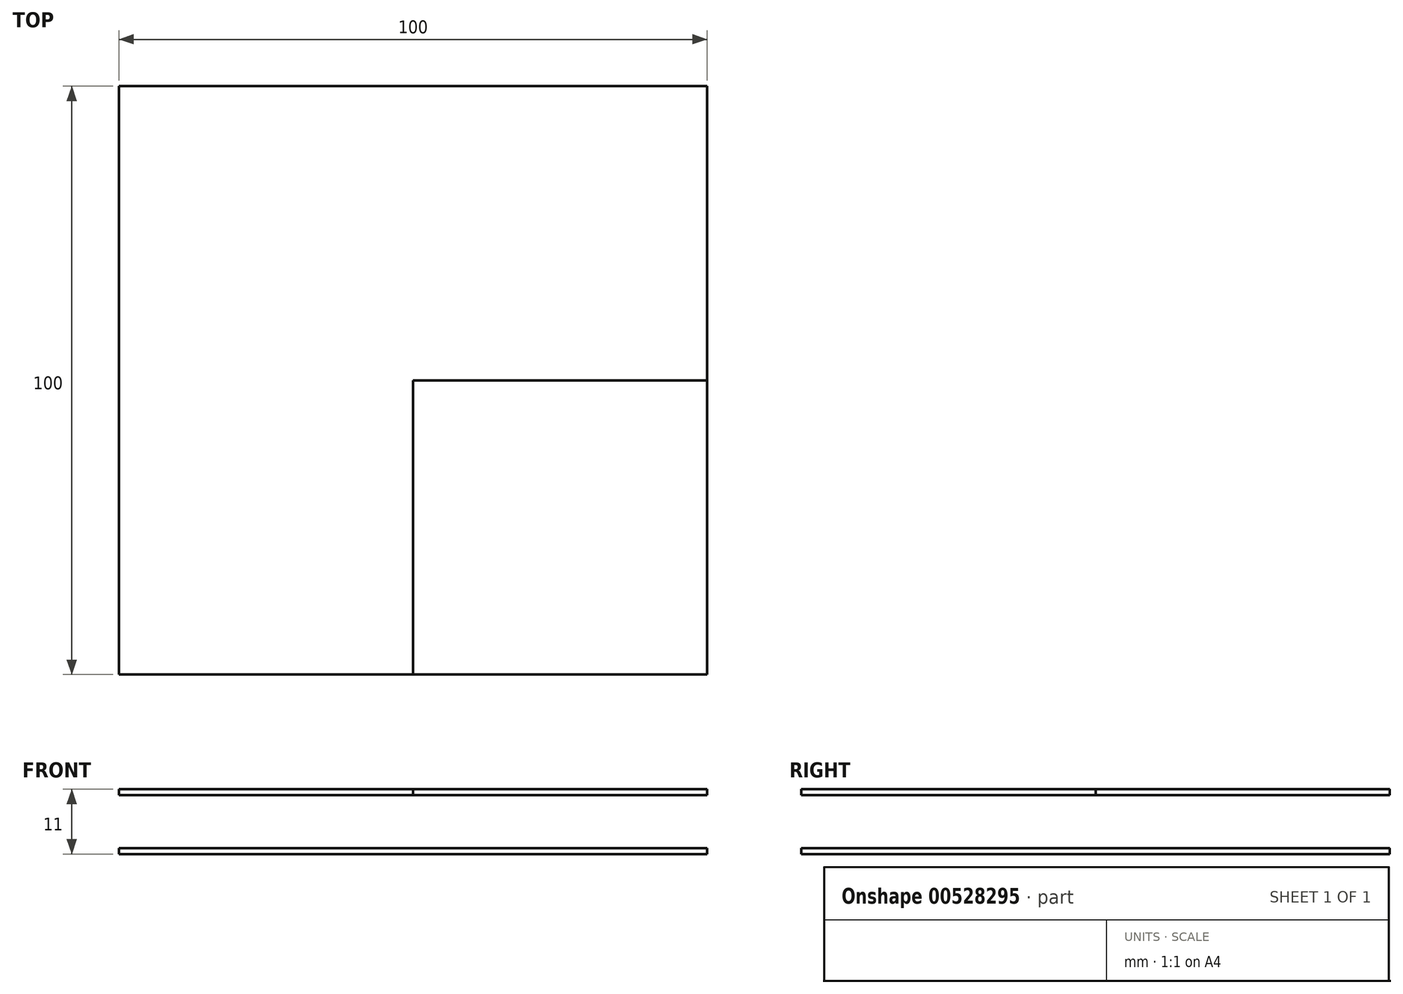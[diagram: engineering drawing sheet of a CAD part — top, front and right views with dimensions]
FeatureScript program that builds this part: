
annotation { "Feature Type Name" : "Feature", "Feature Type Description" : "" }
export const myFeature = defineFeature(function(context is Context, id is Id, definition is map)
    precondition{}
    {
        {
            var Q0;
            Q0=qCreatedBy(makeId("Top.planeOp"),FACE);
            var sketch = newSketch(context, id + "F0", { "sketchPlane" : qUnion([Q0])});
            skLineSegment(sketch, "E0.bottom", {"start": v(0, 0) * mm, "end": v(100, 0) * mm});
            skLineSegment(sketch, "E0.top", {"start": v(0, 100) * mm, "end": v(100, 100) * mm});
            skLineSegment(sketch, "E0.left", {"start": v(0, 0) * mm, "end": v(0, 100) * mm});
            skLineSegment(sketch, "E0.right", {"start": v(100, 0) * mm, "end": v(100, 100) * mm});
            skSolve(sketch);
        }
        {
            var Q0;
            Q0 = qSketchRegion(id + "F0", true);
            extrude(context, id + "F1", {"entities" : qUnion([Q0]), "depth" : 1 * mm, "offsetDistance" : 25 * mm});
        }
        {
            var Q0;
            Q0=qCreatedBy(makeId("Top.planeOp"),FACE);
            cPlane(context, id + "F2", {"entities" : qUnion([Q0]), "cplaneType" : CPlaneType.OFFSET, "offset" : 10 * mm, "width" : 150 * mm, "height" : 150 * mm});
        }
        {
            var Q0;
            Q0=qCreatedBy(id+"F2.planeOp",FACE);
            var sketch = newSketch(context, id + "F3", { "sketchPlane" : qUnion([Q0])});
            skLineSegment(sketch, "E1.bottom", {"start": v(0, 0) * mm, "end": v(100, 0) * mm});
            skLineSegment(sketch, "E1.top", {"start": v(0, 100) * mm, "end": v(100, 100) * mm});
            skLineSegment(sketch, "E1.left", {"start": v(0, 0) * mm, "end": v(0, 100) * mm});
            skLineSegment(sketch, "E1.right", {"start": v(100, 0) * mm, "end": v(100, 100) * mm});
            skLineSegment(sketch, "E2", {"start": v(50, 100) * mm, "end": v(50, 0) * mm});
            skLineSegment(sketch, "E3", {"start": v(0, 50) * mm, "end": v(100, 50) * mm});
            skSolve(sketch);
        }
        {
            var Q0;
            {var subQ0=sQuery(id+"F3.wireOp",EDGE,"E1.left");var subQ1=sQuery(id+"F3.wireOp",EDGE,"E1.bottom");var subQ2=makeQuery(id+"F3.imprint","INTERSECT",VERTEX,{"derivedFrom":[subQ1,subQ0]});Q0=makeQuery(id+"F3.imprint","IMPRINT",FACE,{"disambiguationData":[TD([[makeQuery(id+"F3.imprint","IMPRINT",EDGE,{"disambiguationData":[TD([[subQ2,-1.0]])],"derivedFrom":subQ1}),1.0]])]});}
            var Q1;
            {var subQ0=sQuery(id+"F3.wireOp",EDGE,"E1.left");var subQ1=sQuery(id+"F3.wireOp",EDGE,"E1.top");var subQ2=makeQuery(id+"F3.imprint","INTERSECT",VERTEX,{"derivedFrom":[subQ1,subQ0]});Q1=makeQuery(id+"F3.imprint","IMPRINT",FACE,{"disambiguationData":[TD([[makeQuery(id+"F3.imprint","IMPRINT",EDGE,{"disambiguationData":[TD([[subQ2,-1.0]])],"derivedFrom":subQ1}),-1.0]])]});}
            var Q2;
            {var subQ0=sQuery(id+"F3.wireOp",EDGE,"E1.right");var subQ1=sQuery(id+"F3.wireOp",EDGE,"E1.top");var subQ2=makeQuery(id+"F3.imprint","INTERSECT",VERTEX,{"derivedFrom":[subQ1,subQ0]});Q2=makeQuery(id+"F3.imprint","IMPRINT",FACE,{"disambiguationData":[TD([[makeQuery(id+"F3.imprint","IMPRINT",EDGE,{"disambiguationData":[TD([[subQ2,1.0]])],"derivedFrom":subQ1}),-1.0]])]});}
            extrude(context, id + "F4", {"entities" : qUnion([Q0, Q1, Q2]), "depth" : 1 * mm, "offsetDistance" : 25 * mm});
        }
        {
            var Q0;
            Q0=makeQuery(id+"F1.opExtrude","CAP_FACE",FACE,{"disambiguationData":[OSD([sQuery(id+"F0.wireOp",EDGE,"E0.bottom"),sQuery(id+"F0.wireOp",EDGE,"E0.top"),sQuery(id+"F0.wireOp",EDGE,"E0.left"),sQuery(id+"F0.wireOp",EDGE,"E0.right")])],"isStart":false});
            var sketch = newSketch(context, id + "F5", { "sketchPlane" : qUnion([Q0])});
            skLineSegment(sketch, "E4.bottom", {"start": v(96.5, 6.5) * mm, "end": v(93.5, 6.5) * mm});
            skLineSegment(sketch, "E4.top", {"start": v(96.5, 3.5) * mm, "end": v(93.5, 3.5) * mm});
            skLineSegment(sketch, "E4.left", {"start": v(96.5, 6.5) * mm, "end": v(96.5, 3.5) * mm});
            skLineSegment(sketch, "E4.right", {"start": v(93.5, 6.5) * mm, "end": v(93.5, 3.5) * mm});
            skPoint(sketch, "E4.middle", {"position": v(95, 5) * mm});
            skPoint(sketch, "E5.0.1.0", {"position": v(95, 15) * mm});
            skLineSegment(sketch, "E5.0.1.1", {"start": v(96.5, 16.5) * mm, "end": v(96.5, 13.5) * mm});
            skLineSegment(sketch, "E5.0.1.2", {"start": v(96.5, 16.5) * mm, "end": v(93.5, 16.5) * mm});
            skLineSegment(sketch, "E5.0.1.3", {"start": v(93.5, 16.5) * mm, "end": v(93.5, 13.5) * mm});
            skLineSegment(sketch, "E5.0.1.4", {"start": v(96.5, 13.5) * mm, "end": v(93.5, 13.5) * mm});
            skPoint(sketch, "E5.0.2.0", {"position": v(95, 25) * mm});
            skLineSegment(sketch, "E5.0.2.1", {"start": v(96.5, 26.5) * mm, "end": v(96.5, 23.5) * mm});
            skLineSegment(sketch, "E5.0.2.2", {"start": v(96.5, 26.5) * mm, "end": v(93.5, 26.5) * mm});
            skLineSegment(sketch, "E5.0.2.3", {"start": v(93.5, 26.5) * mm, "end": v(93.5, 23.5) * mm});
            skLineSegment(sketch, "E5.0.2.4", {"start": v(96.5, 23.5) * mm, "end": v(93.5, 23.5) * mm});
            skPoint(sketch, "E5.0.3.0", {"position": v(95, 35) * mm});
            skLineSegment(sketch, "E5.0.3.1", {"start": v(96.5, 36.5) * mm, "end": v(96.5, 33.5) * mm});
            skLineSegment(sketch, "E5.0.3.2", {"start": v(96.5, 36.5) * mm, "end": v(93.5, 36.5) * mm});
            skLineSegment(sketch, "E5.0.3.3", {"start": v(93.5, 36.5) * mm, "end": v(93.5, 33.5) * mm});
            skLineSegment(sketch, "E5.0.3.4", {"start": v(96.5, 33.5) * mm, "end": v(93.5, 33.5) * mm});
            skPoint(sketch, "E5.0.4.0", {"position": v(95, 45) * mm});
            skLineSegment(sketch, "E5.0.4.1", {"start": v(96.5, 46.5) * mm, "end": v(96.5, 43.5) * mm});
            skLineSegment(sketch, "E5.0.4.2", {"start": v(96.5, 46.5) * mm, "end": v(93.5, 46.5) * mm});
            skLineSegment(sketch, "E5.0.4.3", {"start": v(93.5, 46.5) * mm, "end": v(93.5, 43.5) * mm});
            skLineSegment(sketch, "E5.0.4.4", {"start": v(96.5, 43.5) * mm, "end": v(93.5, 43.5) * mm});
            skPoint(sketch, "E5.0.5.0", {"position": v(95, 55) * mm});
            skLineSegment(sketch, "E5.0.5.1", {"start": v(96.5, 56.5) * mm, "end": v(96.5, 53.5) * mm});
            skLineSegment(sketch, "E5.0.5.2", {"start": v(96.5, 56.5) * mm, "end": v(93.5, 56.5) * mm});
            skLineSegment(sketch, "E5.0.5.3", {"start": v(93.5, 56.5) * mm, "end": v(93.5, 53.5) * mm});
            skLineSegment(sketch, "E5.0.5.4", {"start": v(96.5, 53.5) * mm, "end": v(93.5, 53.5) * mm});
            skPoint(sketch, "E5.0.6.0", {"position": v(95, 65) * mm});
            skLineSegment(sketch, "E5.0.6.1", {"start": v(96.5, 66.5) * mm, "end": v(96.5, 63.5) * mm});
            skLineSegment(sketch, "E5.0.6.2", {"start": v(96.5, 66.5) * mm, "end": v(93.5, 66.5) * mm});
            skLineSegment(sketch, "E5.0.6.3", {"start": v(93.5, 66.5) * mm, "end": v(93.5, 63.5) * mm});
            skLineSegment(sketch, "E5.0.6.4", {"start": v(96.5, 63.5) * mm, "end": v(93.5, 63.5) * mm});
            skPoint(sketch, "E5.0.7.0", {"position": v(95, 75) * mm});
            skLineSegment(sketch, "E5.0.7.1", {"start": v(96.5, 76.5) * mm, "end": v(96.5, 73.5) * mm});
            skLineSegment(sketch, "E5.0.7.2", {"start": v(96.5, 76.5) * mm, "end": v(93.5, 76.5) * mm});
            skLineSegment(sketch, "E5.0.7.3", {"start": v(93.5, 76.5) * mm, "end": v(93.5, 73.5) * mm});
            skLineSegment(sketch, "E5.0.7.4", {"start": v(96.5, 73.5) * mm, "end": v(93.5, 73.5) * mm});
            skPoint(sketch, "E5.0.8.0", {"position": v(95, 85) * mm});
            skLineSegment(sketch, "E5.0.8.1", {"start": v(96.5, 86.5) * mm, "end": v(96.5, 83.5) * mm});
            skLineSegment(sketch, "E5.0.8.2", {"start": v(96.5, 86.5) * mm, "end": v(93.5, 86.5) * mm});
            skLineSegment(sketch, "E5.0.8.3", {"start": v(93.5, 86.5) * mm, "end": v(93.5, 83.5) * mm});
            skLineSegment(sketch, "E5.0.8.4", {"start": v(96.5, 83.5) * mm, "end": v(93.5, 83.5) * mm});
            skPoint(sketch, "E5.1.0.0", {"position": v(85, 5) * mm});
            skLineSegment(sketch, "E5.1.0.1", {"start": v(86.5, 6.5) * mm, "end": v(86.5, 3.5) * mm});
            skLineSegment(sketch, "E5.1.0.2", {"start": v(86.5, 6.5) * mm, "end": v(83.5, 6.5) * mm});
            skLineSegment(sketch, "E5.1.0.3", {"start": v(83.5, 6.5) * mm, "end": v(83.5, 3.5) * mm});
            skLineSegment(sketch, "E5.1.0.4", {"start": v(86.5, 3.5) * mm, "end": v(83.5, 3.5) * mm});
            skPoint(sketch, "E5.1.1.0", {"position": v(85, 15) * mm});
            skLineSegment(sketch, "E5.1.1.1", {"start": v(86.5, 16.5) * mm, "end": v(86.5, 13.5) * mm});
            skLineSegment(sketch, "E5.1.1.2", {"start": v(86.5, 16.5) * mm, "end": v(83.5, 16.5) * mm});
            skLineSegment(sketch, "E5.1.1.3", {"start": v(83.5, 16.5) * mm, "end": v(83.5, 13.5) * mm});
            skLineSegment(sketch, "E5.1.1.4", {"start": v(86.5, 13.5) * mm, "end": v(83.5, 13.5) * mm});
            skPoint(sketch, "E5.1.2.0", {"position": v(85, 25) * mm});
            skLineSegment(sketch, "E5.1.2.1", {"start": v(86.5, 26.5) * mm, "end": v(86.5, 23.5) * mm});
            skLineSegment(sketch, "E5.1.2.2", {"start": v(86.5, 26.5) * mm, "end": v(83.5, 26.5) * mm});
            skLineSegment(sketch, "E5.1.2.3", {"start": v(83.5, 26.5) * mm, "end": v(83.5, 23.5) * mm});
            skLineSegment(sketch, "E5.1.2.4", {"start": v(86.5, 23.5) * mm, "end": v(83.5, 23.5) * mm});
            skPoint(sketch, "E5.1.3.0", {"position": v(85, 35) * mm});
            skLineSegment(sketch, "E5.1.3.1", {"start": v(86.5, 36.5) * mm, "end": v(86.5, 33.5) * mm});
            skLineSegment(sketch, "E5.1.3.2", {"start": v(86.5, 36.5) * mm, "end": v(83.5, 36.5) * mm});
            skLineSegment(sketch, "E5.1.3.3", {"start": v(83.5, 36.5) * mm, "end": v(83.5, 33.5) * mm});
            skLineSegment(sketch, "E5.1.3.4", {"start": v(86.5, 33.5) * mm, "end": v(83.5, 33.5) * mm});
            skPoint(sketch, "E5.1.4.0", {"position": v(85, 45) * mm});
            skLineSegment(sketch, "E5.1.4.1", {"start": v(86.5, 46.5) * mm, "end": v(86.5, 43.5) * mm});
            skLineSegment(sketch, "E5.1.4.2", {"start": v(86.5, 46.5) * mm, "end": v(83.5, 46.5) * mm});
            skLineSegment(sketch, "E5.1.4.3", {"start": v(83.5, 46.5) * mm, "end": v(83.5, 43.5) * mm});
            skLineSegment(sketch, "E5.1.4.4", {"start": v(86.5, 43.5) * mm, "end": v(83.5, 43.5) * mm});
            skPoint(sketch, "E5.1.5.0", {"position": v(85, 55) * mm});
            skLineSegment(sketch, "E5.1.5.1", {"start": v(86.5, 56.5) * mm, "end": v(86.5, 53.5) * mm});
            skLineSegment(sketch, "E5.1.5.2", {"start": v(86.5, 56.5) * mm, "end": v(83.5, 56.5) * mm});
            skLineSegment(sketch, "E5.1.5.3", {"start": v(83.5, 56.5) * mm, "end": v(83.5, 53.5) * mm});
            skLineSegment(sketch, "E5.1.5.4", {"start": v(86.5, 53.5) * mm, "end": v(83.5, 53.5) * mm});
            skPoint(sketch, "E5.1.6.0", {"position": v(85, 65) * mm});
            skLineSegment(sketch, "E5.1.6.1", {"start": v(86.5, 66.5) * mm, "end": v(86.5, 63.5) * mm});
            skLineSegment(sketch, "E5.1.6.2", {"start": v(86.5, 66.5) * mm, "end": v(83.5, 66.5) * mm});
            skLineSegment(sketch, "E5.1.6.3", {"start": v(83.5, 66.5) * mm, "end": v(83.5, 63.5) * mm});
            skLineSegment(sketch, "E5.1.6.4", {"start": v(86.5, 63.5) * mm, "end": v(83.5, 63.5) * mm});
            skPoint(sketch, "E5.1.7.0", {"position": v(85, 75) * mm});
            skLineSegment(sketch, "E5.1.7.1", {"start": v(86.5, 76.5) * mm, "end": v(86.5, 73.5) * mm});
            skLineSegment(sketch, "E5.1.7.2", {"start": v(86.5, 76.5) * mm, "end": v(83.5, 76.5) * mm});
            skLineSegment(sketch, "E5.1.7.3", {"start": v(83.5, 76.5) * mm, "end": v(83.5, 73.5) * mm});
            skLineSegment(sketch, "E5.1.7.4", {"start": v(86.5, 73.5) * mm, "end": v(83.5, 73.5) * mm});
            skPoint(sketch, "E5.1.8.0", {"position": v(85, 85) * mm});
            skLineSegment(sketch, "E5.1.8.1", {"start": v(86.5, 86.5) * mm, "end": v(86.5, 83.5) * mm});
            skLineSegment(sketch, "E5.1.8.2", {"start": v(86.5, 86.5) * mm, "end": v(83.5, 86.5) * mm});
            skLineSegment(sketch, "E5.1.8.3", {"start": v(83.5, 86.5) * mm, "end": v(83.5, 83.5) * mm});
            skLineSegment(sketch, "E5.1.8.4", {"start": v(86.5, 83.5) * mm, "end": v(83.5, 83.5) * mm});
            skPoint(sketch, "E5.2.0.0", {"position": v(75, 5) * mm});
            skLineSegment(sketch, "E5.2.0.1", {"start": v(76.5, 6.5) * mm, "end": v(76.5, 3.5) * mm});
            skLineSegment(sketch, "E5.2.0.2", {"start": v(76.5, 6.5) * mm, "end": v(73.5, 6.5) * mm});
            skLineSegment(sketch, "E5.2.0.3", {"start": v(73.5, 6.5) * mm, "end": v(73.5, 3.5) * mm});
            skLineSegment(sketch, "E5.2.0.4", {"start": v(76.5, 3.5) * mm, "end": v(73.5, 3.5) * mm});
            skPoint(sketch, "E5.2.1.0", {"position": v(75, 15) * mm});
            skLineSegment(sketch, "E5.2.1.1", {"start": v(76.5, 16.5) * mm, "end": v(76.5, 13.5) * mm});
            skLineSegment(sketch, "E5.2.1.2", {"start": v(76.5, 16.5) * mm, "end": v(73.5, 16.5) * mm});
            skLineSegment(sketch, "E5.2.1.3", {"start": v(73.5, 16.5) * mm, "end": v(73.5, 13.5) * mm});
            skLineSegment(sketch, "E5.2.1.4", {"start": v(76.5, 13.5) * mm, "end": v(73.5, 13.5) * mm});
            skPoint(sketch, "E5.2.2.0", {"position": v(75, 25) * mm});
            skLineSegment(sketch, "E5.2.2.1", {"start": v(76.5, 26.5) * mm, "end": v(76.5, 23.5) * mm});
            skLineSegment(sketch, "E5.2.2.2", {"start": v(76.5, 26.5) * mm, "end": v(73.5, 26.5) * mm});
            skLineSegment(sketch, "E5.2.2.3", {"start": v(73.5, 26.5) * mm, "end": v(73.5, 23.5) * mm});
            skLineSegment(sketch, "E5.2.2.4", {"start": v(76.5, 23.5) * mm, "end": v(73.5, 23.5) * mm});
            skPoint(sketch, "E5.2.3.0", {"position": v(75, 35) * mm});
            skLineSegment(sketch, "E5.2.3.1", {"start": v(76.5, 36.5) * mm, "end": v(76.5, 33.5) * mm});
            skLineSegment(sketch, "E5.2.3.2", {"start": v(76.5, 36.5) * mm, "end": v(73.5, 36.5) * mm});
            skLineSegment(sketch, "E5.2.3.3", {"start": v(73.5, 36.5) * mm, "end": v(73.5, 33.5) * mm});
            skLineSegment(sketch, "E5.2.3.4", {"start": v(76.5, 33.5) * mm, "end": v(73.5, 33.5) * mm});
            skPoint(sketch, "E5.2.4.0", {"position": v(75, 45) * mm});
            skLineSegment(sketch, "E5.2.4.1", {"start": v(76.5, 46.5) * mm, "end": v(76.5, 43.5) * mm});
            skLineSegment(sketch, "E5.2.4.2", {"start": v(76.5, 46.5) * mm, "end": v(73.5, 46.5) * mm});
            skLineSegment(sketch, "E5.2.4.3", {"start": v(73.5, 46.5) * mm, "end": v(73.5, 43.5) * mm});
            skLineSegment(sketch, "E5.2.4.4", {"start": v(76.5, 43.5) * mm, "end": v(73.5, 43.5) * mm});
            skPoint(sketch, "E5.2.5.0", {"position": v(75, 55) * mm});
            skLineSegment(sketch, "E5.2.5.1", {"start": v(76.5, 56.5) * mm, "end": v(76.5, 53.5) * mm});
            skLineSegment(sketch, "E5.2.5.2", {"start": v(76.5, 56.5) * mm, "end": v(73.5, 56.5) * mm});
            skLineSegment(sketch, "E5.2.5.3", {"start": v(73.5, 56.5) * mm, "end": v(73.5, 53.5) * mm});
            skLineSegment(sketch, "E5.2.5.4", {"start": v(76.5, 53.5) * mm, "end": v(73.5, 53.5) * mm});
            skPoint(sketch, "E5.2.6.0", {"position": v(75, 65) * mm});
            skLineSegment(sketch, "E5.2.6.1", {"start": v(76.5, 66.5) * mm, "end": v(76.5, 63.5) * mm});
            skLineSegment(sketch, "E5.2.6.2", {"start": v(76.5, 66.5) * mm, "end": v(73.5, 66.5) * mm});
            skLineSegment(sketch, "E5.2.6.3", {"start": v(73.5, 66.5) * mm, "end": v(73.5, 63.5) * mm});
            skLineSegment(sketch, "E5.2.6.4", {"start": v(76.5, 63.5) * mm, "end": v(73.5, 63.5) * mm});
            skPoint(sketch, "E5.2.7.0", {"position": v(75, 75) * mm});
            skLineSegment(sketch, "E5.2.7.1", {"start": v(76.5, 76.5) * mm, "end": v(76.5, 73.5) * mm});
            skLineSegment(sketch, "E5.2.7.2", {"start": v(76.5, 76.5) * mm, "end": v(73.5, 76.5) * mm});
            skLineSegment(sketch, "E5.2.7.3", {"start": v(73.5, 76.5) * mm, "end": v(73.5, 73.5) * mm});
            skLineSegment(sketch, "E5.2.7.4", {"start": v(76.5, 73.5) * mm, "end": v(73.5, 73.5) * mm});
            skPoint(sketch, "E5.2.8.0", {"position": v(75, 85) * mm});
            skLineSegment(sketch, "E5.2.8.1", {"start": v(76.5, 86.5) * mm, "end": v(76.5, 83.5) * mm});
            skLineSegment(sketch, "E5.2.8.2", {"start": v(76.5, 86.5) * mm, "end": v(73.5, 86.5) * mm});
            skLineSegment(sketch, "E5.2.8.3", {"start": v(73.5, 86.5) * mm, "end": v(73.5, 83.5) * mm});
            skLineSegment(sketch, "E5.2.8.4", {"start": v(76.5, 83.5) * mm, "end": v(73.5, 83.5) * mm});
            skPoint(sketch, "E5.3.0.0", {"position": v(65, 5) * mm});
            skLineSegment(sketch, "E5.3.0.1", {"start": v(66.5, 6.5) * mm, "end": v(66.5, 3.5) * mm});
            skLineSegment(sketch, "E5.3.0.2", {"start": v(66.5, 6.5) * mm, "end": v(63.5, 6.5) * mm});
            skLineSegment(sketch, "E5.3.0.3", {"start": v(63.5, 6.5) * mm, "end": v(63.5, 3.5) * mm});
            skLineSegment(sketch, "E5.3.0.4", {"start": v(66.5, 3.5) * mm, "end": v(63.5, 3.5) * mm});
            skPoint(sketch, "E5.3.1.0", {"position": v(65, 15) * mm});
            skLineSegment(sketch, "E5.3.1.1", {"start": v(66.5, 16.5) * mm, "end": v(66.5, 13.5) * mm});
            skLineSegment(sketch, "E5.3.1.2", {"start": v(66.5, 16.5) * mm, "end": v(63.5, 16.5) * mm});
            skLineSegment(sketch, "E5.3.1.3", {"start": v(63.5, 16.5) * mm, "end": v(63.5, 13.5) * mm});
            skLineSegment(sketch, "E5.3.1.4", {"start": v(66.5, 13.5) * mm, "end": v(63.5, 13.5) * mm});
            skPoint(sketch, "E5.3.2.0", {"position": v(65, 25) * mm});
            skLineSegment(sketch, "E5.3.2.1", {"start": v(66.5, 26.5) * mm, "end": v(66.5, 23.5) * mm});
            skLineSegment(sketch, "E5.3.2.2", {"start": v(66.5, 26.5) * mm, "end": v(63.5, 26.5) * mm});
            skLineSegment(sketch, "E5.3.2.3", {"start": v(63.5, 26.5) * mm, "end": v(63.5, 23.5) * mm});
            skLineSegment(sketch, "E5.3.2.4", {"start": v(66.5, 23.5) * mm, "end": v(63.5, 23.5) * mm});
            skPoint(sketch, "E5.3.3.0", {"position": v(65, 35) * mm});
            skLineSegment(sketch, "E5.3.3.1", {"start": v(66.5, 36.5) * mm, "end": v(66.5, 33.5) * mm});
            skLineSegment(sketch, "E5.3.3.2", {"start": v(66.5, 36.5) * mm, "end": v(63.5, 36.5) * mm});
            skLineSegment(sketch, "E5.3.3.3", {"start": v(63.5, 36.5) * mm, "end": v(63.5, 33.5) * mm});
            skLineSegment(sketch, "E5.3.3.4", {"start": v(66.5, 33.5) * mm, "end": v(63.5, 33.5) * mm});
            skPoint(sketch, "E5.3.4.0", {"position": v(65, 45) * mm});
            skLineSegment(sketch, "E5.3.4.1", {"start": v(66.5, 46.5) * mm, "end": v(66.5, 43.5) * mm});
            skLineSegment(sketch, "E5.3.4.2", {"start": v(66.5, 46.5) * mm, "end": v(63.5, 46.5) * mm});
            skLineSegment(sketch, "E5.3.4.3", {"start": v(63.5, 46.5) * mm, "end": v(63.5, 43.5) * mm});
            skLineSegment(sketch, "E5.3.4.4", {"start": v(66.5, 43.5) * mm, "end": v(63.5, 43.5) * mm});
            skPoint(sketch, "E5.3.5.0", {"position": v(65, 55) * mm});
            skLineSegment(sketch, "E5.3.5.1", {"start": v(66.5, 56.5) * mm, "end": v(66.5, 53.5) * mm});
            skLineSegment(sketch, "E5.3.5.2", {"start": v(66.5, 56.5) * mm, "end": v(63.5, 56.5) * mm});
            skLineSegment(sketch, "E5.3.5.3", {"start": v(63.5, 56.5) * mm, "end": v(63.5, 53.5) * mm});
            skLineSegment(sketch, "E5.3.5.4", {"start": v(66.5, 53.5) * mm, "end": v(63.5, 53.5) * mm});
            skPoint(sketch, "E5.3.6.0", {"position": v(65, 65) * mm});
            skLineSegment(sketch, "E5.3.6.1", {"start": v(66.5, 66.5) * mm, "end": v(66.5, 63.5) * mm});
            skLineSegment(sketch, "E5.3.6.2", {"start": v(66.5, 66.5) * mm, "end": v(63.5, 66.5) * mm});
            skLineSegment(sketch, "E5.3.6.3", {"start": v(63.5, 66.5) * mm, "end": v(63.5, 63.5) * mm});
            skLineSegment(sketch, "E5.3.6.4", {"start": v(66.5, 63.5) * mm, "end": v(63.5, 63.5) * mm});
            skPoint(sketch, "E5.3.7.0", {"position": v(65, 75) * mm});
            skLineSegment(sketch, "E5.3.7.1", {"start": v(66.5, 76.5) * mm, "end": v(66.5, 73.5) * mm});
            skLineSegment(sketch, "E5.3.7.2", {"start": v(66.5, 76.5) * mm, "end": v(63.5, 76.5) * mm});
            skLineSegment(sketch, "E5.3.7.3", {"start": v(63.5, 76.5) * mm, "end": v(63.5, 73.5) * mm});
            skLineSegment(sketch, "E5.3.7.4", {"start": v(66.5, 73.5) * mm, "end": v(63.5, 73.5) * mm});
            skPoint(sketch, "E5.3.8.0", {"position": v(65, 85) * mm});
            skLineSegment(sketch, "E5.3.8.1", {"start": v(66.5, 86.5) * mm, "end": v(66.5, 83.5) * mm});
            skLineSegment(sketch, "E5.3.8.2", {"start": v(66.5, 86.5) * mm, "end": v(63.5, 86.5) * mm});
            skLineSegment(sketch, "E5.3.8.3", {"start": v(63.5, 86.5) * mm, "end": v(63.5, 83.5) * mm});
            skLineSegment(sketch, "E5.3.8.4", {"start": v(66.5, 83.5) * mm, "end": v(63.5, 83.5) * mm});
            skPoint(sketch, "E5.4.0.0", {"position": v(55, 5) * mm});
            skLineSegment(sketch, "E5.4.0.1", {"start": v(56.5, 6.5) * mm, "end": v(56.5, 3.5) * mm});
            skLineSegment(sketch, "E5.4.0.2", {"start": v(56.5, 6.5) * mm, "end": v(53.5, 6.5) * mm});
            skLineSegment(sketch, "E5.4.0.3", {"start": v(53.5, 6.5) * mm, "end": v(53.5, 3.5) * mm});
            skLineSegment(sketch, "E5.4.0.4", {"start": v(56.5, 3.5) * mm, "end": v(53.5, 3.5) * mm});
            skPoint(sketch, "E5.4.1.0", {"position": v(55, 15) * mm});
            skLineSegment(sketch, "E5.4.1.1", {"start": v(56.5, 16.5) * mm, "end": v(56.5, 13.5) * mm});
            skLineSegment(sketch, "E5.4.1.2", {"start": v(56.5, 16.5) * mm, "end": v(53.5, 16.5) * mm});
            skLineSegment(sketch, "E5.4.1.3", {"start": v(53.5, 16.5) * mm, "end": v(53.5, 13.5) * mm});
            skLineSegment(sketch, "E5.4.1.4", {"start": v(56.5, 13.5) * mm, "end": v(53.5, 13.5) * mm});
            skPoint(sketch, "E5.4.2.0", {"position": v(55, 25) * mm});
            skLineSegment(sketch, "E5.4.2.1", {"start": v(56.5, 26.5) * mm, "end": v(56.5, 23.5) * mm});
            skLineSegment(sketch, "E5.4.2.2", {"start": v(56.5, 26.5) * mm, "end": v(53.5, 26.5) * mm});
            skLineSegment(sketch, "E5.4.2.3", {"start": v(53.5, 26.5) * mm, "end": v(53.5, 23.5) * mm});
            skLineSegment(sketch, "E5.4.2.4", {"start": v(56.5, 23.5) * mm, "end": v(53.5, 23.5) * mm});
            skPoint(sketch, "E5.4.3.0", {"position": v(55, 35) * mm});
            skLineSegment(sketch, "E5.4.3.1", {"start": v(56.5, 36.5) * mm, "end": v(56.5, 33.5) * mm});
            skLineSegment(sketch, "E5.4.3.2", {"start": v(56.5, 36.5) * mm, "end": v(53.5, 36.5) * mm});
            skLineSegment(sketch, "E5.4.3.3", {"start": v(53.5, 36.5) * mm, "end": v(53.5, 33.5) * mm});
            skLineSegment(sketch, "E5.4.3.4", {"start": v(56.5, 33.5) * mm, "end": v(53.5, 33.5) * mm});
            skPoint(sketch, "E5.4.4.0", {"position": v(55, 45) * mm});
            skLineSegment(sketch, "E5.4.4.1", {"start": v(56.5, 46.5) * mm, "end": v(56.5, 43.5) * mm});
            skLineSegment(sketch, "E5.4.4.2", {"start": v(56.5, 46.5) * mm, "end": v(53.5, 46.5) * mm});
            skLineSegment(sketch, "E5.4.4.3", {"start": v(53.5, 46.5) * mm, "end": v(53.5, 43.5) * mm});
            skLineSegment(sketch, "E5.4.4.4", {"start": v(56.5, 43.5) * mm, "end": v(53.5, 43.5) * mm});
            skPoint(sketch, "E5.4.5.0", {"position": v(55, 55) * mm});
            skLineSegment(sketch, "E5.4.5.1", {"start": v(56.5, 56.5) * mm, "end": v(56.5, 53.5) * mm});
            skLineSegment(sketch, "E5.4.5.2", {"start": v(56.5, 56.5) * mm, "end": v(53.5, 56.5) * mm});
            skLineSegment(sketch, "E5.4.5.3", {"start": v(53.5, 56.5) * mm, "end": v(53.5, 53.5) * mm});
            skLineSegment(sketch, "E5.4.5.4", {"start": v(56.5, 53.5) * mm, "end": v(53.5, 53.5) * mm});
            skPoint(sketch, "E5.4.6.0", {"position": v(55, 65) * mm});
            skLineSegment(sketch, "E5.4.6.1", {"start": v(56.5, 66.5) * mm, "end": v(56.5, 63.5) * mm});
            skLineSegment(sketch, "E5.4.6.2", {"start": v(56.5, 66.5) * mm, "end": v(53.5, 66.5) * mm});
            skLineSegment(sketch, "E5.4.6.3", {"start": v(53.5, 66.5) * mm, "end": v(53.5, 63.5) * mm});
            skLineSegment(sketch, "E5.4.6.4", {"start": v(56.5, 63.5) * mm, "end": v(53.5, 63.5) * mm});
            skPoint(sketch, "E5.4.7.0", {"position": v(55, 75) * mm});
            skLineSegment(sketch, "E5.4.7.1", {"start": v(56.5, 76.5) * mm, "end": v(56.5, 73.5) * mm});
            skLineSegment(sketch, "E5.4.7.2", {"start": v(56.5, 76.5) * mm, "end": v(53.5, 76.5) * mm});
            skLineSegment(sketch, "E5.4.7.3", {"start": v(53.5, 76.5) * mm, "end": v(53.5, 73.5) * mm});
            skLineSegment(sketch, "E5.4.7.4", {"start": v(56.5, 73.5) * mm, "end": v(53.5, 73.5) * mm});
            skPoint(sketch, "E5.4.8.0", {"position": v(55, 85) * mm});
            skLineSegment(sketch, "E5.4.8.1", {"start": v(56.5, 86.5) * mm, "end": v(56.5, 83.5) * mm});
            skLineSegment(sketch, "E5.4.8.2", {"start": v(56.5, 86.5) * mm, "end": v(53.5, 86.5) * mm});
            skLineSegment(sketch, "E5.4.8.3", {"start": v(53.5, 86.5) * mm, "end": v(53.5, 83.5) * mm});
            skLineSegment(sketch, "E5.4.8.4", {"start": v(56.5, 83.5) * mm, "end": v(53.5, 83.5) * mm});
            skPoint(sketch, "E5.5.0.0", {"position": v(45, 5) * mm});
            skLineSegment(sketch, "E5.5.0.1", {"start": v(46.5, 6.5) * mm, "end": v(46.5, 3.5) * mm});
            skLineSegment(sketch, "E5.5.0.2", {"start": v(46.5, 6.5) * mm, "end": v(43.5, 6.5) * mm});
            skLineSegment(sketch, "E5.5.0.3", {"start": v(43.5, 6.5) * mm, "end": v(43.5, 3.5) * mm});
            skLineSegment(sketch, "E5.5.0.4", {"start": v(46.5, 3.5) * mm, "end": v(43.5, 3.5) * mm});
            skPoint(sketch, "E5.5.1.0", {"position": v(45, 15) * mm});
            skLineSegment(sketch, "E5.5.1.1", {"start": v(46.5, 16.5) * mm, "end": v(46.5, 13.5) * mm});
            skLineSegment(sketch, "E5.5.1.2", {"start": v(46.5, 16.5) * mm, "end": v(43.5, 16.5) * mm});
            skLineSegment(sketch, "E5.5.1.3", {"start": v(43.5, 16.5) * mm, "end": v(43.5, 13.5) * mm});
            skLineSegment(sketch, "E5.5.1.4", {"start": v(46.5, 13.5) * mm, "end": v(43.5, 13.5) * mm});
            skPoint(sketch, "E5.5.2.0", {"position": v(45, 25) * mm});
            skLineSegment(sketch, "E5.5.2.1", {"start": v(46.5, 26.5) * mm, "end": v(46.5, 23.5) * mm});
            skLineSegment(sketch, "E5.5.2.2", {"start": v(46.5, 26.5) * mm, "end": v(43.5, 26.5) * mm});
            skLineSegment(sketch, "E5.5.2.3", {"start": v(43.5, 26.5) * mm, "end": v(43.5, 23.5) * mm});
            skLineSegment(sketch, "E5.5.2.4", {"start": v(46.5, 23.5) * mm, "end": v(43.5, 23.5) * mm});
            skPoint(sketch, "E5.5.3.0", {"position": v(45, 35) * mm});
            skLineSegment(sketch, "E5.5.3.1", {"start": v(46.5, 36.5) * mm, "end": v(46.5, 33.5) * mm});
            skLineSegment(sketch, "E5.5.3.2", {"start": v(46.5, 36.5) * mm, "end": v(43.5, 36.5) * mm});
            skLineSegment(sketch, "E5.5.3.3", {"start": v(43.5, 36.5) * mm, "end": v(43.5, 33.5) * mm});
            skLineSegment(sketch, "E5.5.3.4", {"start": v(46.5, 33.5) * mm, "end": v(43.5, 33.5) * mm});
            skPoint(sketch, "E5.5.4.0", {"position": v(45, 45) * mm});
            skLineSegment(sketch, "E5.5.4.1", {"start": v(46.5, 46.5) * mm, "end": v(46.5, 43.5) * mm});
            skLineSegment(sketch, "E5.5.4.2", {"start": v(46.5, 46.5) * mm, "end": v(43.5, 46.5) * mm});
            skLineSegment(sketch, "E5.5.4.3", {"start": v(43.5, 46.5) * mm, "end": v(43.5, 43.5) * mm});
            skLineSegment(sketch, "E5.5.4.4", {"start": v(46.5, 43.5) * mm, "end": v(43.5, 43.5) * mm});
            skPoint(sketch, "E5.5.5.0", {"position": v(45, 55) * mm});
            skLineSegment(sketch, "E5.5.5.1", {"start": v(46.5, 56.5) * mm, "end": v(46.5, 53.5) * mm});
            skLineSegment(sketch, "E5.5.5.2", {"start": v(46.5, 56.5) * mm, "end": v(43.5, 56.5) * mm});
            skLineSegment(sketch, "E5.5.5.3", {"start": v(43.5, 56.5) * mm, "end": v(43.5, 53.5) * mm});
            skLineSegment(sketch, "E5.5.5.4", {"start": v(46.5, 53.5) * mm, "end": v(43.5, 53.5) * mm});
            skPoint(sketch, "E5.5.6.0", {"position": v(45, 65) * mm});
            skLineSegment(sketch, "E5.5.6.1", {"start": v(46.5, 66.5) * mm, "end": v(46.5, 63.5) * mm});
            skLineSegment(sketch, "E5.5.6.2", {"start": v(46.5, 66.5) * mm, "end": v(43.5, 66.5) * mm});
            skLineSegment(sketch, "E5.5.6.3", {"start": v(43.5, 66.5) * mm, "end": v(43.5, 63.5) * mm});
            skLineSegment(sketch, "E5.5.6.4", {"start": v(46.5, 63.5) * mm, "end": v(43.5, 63.5) * mm});
            skPoint(sketch, "E5.5.7.0", {"position": v(45, 75) * mm});
            skLineSegment(sketch, "E5.5.7.1", {"start": v(46.5, 76.5) * mm, "end": v(46.5, 73.5) * mm});
            skLineSegment(sketch, "E5.5.7.2", {"start": v(46.5, 76.5) * mm, "end": v(43.5, 76.5) * mm});
            skLineSegment(sketch, "E5.5.7.3", {"start": v(43.5, 76.5) * mm, "end": v(43.5, 73.5) * mm});
            skLineSegment(sketch, "E5.5.7.4", {"start": v(46.5, 73.5) * mm, "end": v(43.5, 73.5) * mm});
            skPoint(sketch, "E5.5.8.0", {"position": v(45, 85) * mm});
            skLineSegment(sketch, "E5.5.8.1", {"start": v(46.5, 86.5) * mm, "end": v(46.5, 83.5) * mm});
            skLineSegment(sketch, "E5.5.8.2", {"start": v(46.5, 86.5) * mm, "end": v(43.5, 86.5) * mm});
            skLineSegment(sketch, "E5.5.8.3", {"start": v(43.5, 86.5) * mm, "end": v(43.5, 83.5) * mm});
            skLineSegment(sketch, "E5.5.8.4", {"start": v(46.5, 83.5) * mm, "end": v(43.5, 83.5) * mm});
            skPoint(sketch, "E5.6.0.0", {"position": v(35, 5) * mm});
            skLineSegment(sketch, "E5.6.0.1", {"start": v(36.5, 6.5) * mm, "end": v(36.5, 3.5) * mm});
            skLineSegment(sketch, "E5.6.0.2", {"start": v(36.5, 6.5) * mm, "end": v(33.5, 6.5) * mm});
            skLineSegment(sketch, "E5.6.0.3", {"start": v(33.5, 6.5) * mm, "end": v(33.5, 3.5) * mm});
            skLineSegment(sketch, "E5.6.0.4", {"start": v(36.5, 3.5) * mm, "end": v(33.5, 3.5) * mm});
            skPoint(sketch, "E5.6.1.0", {"position": v(35, 15) * mm});
            skLineSegment(sketch, "E5.6.1.1", {"start": v(36.5, 16.5) * mm, "end": v(36.5, 13.5) * mm});
            skLineSegment(sketch, "E5.6.1.2", {"start": v(36.5, 16.5) * mm, "end": v(33.5, 16.5) * mm});
            skLineSegment(sketch, "E5.6.1.3", {"start": v(33.5, 16.5) * mm, "end": v(33.5, 13.5) * mm});
            skLineSegment(sketch, "E5.6.1.4", {"start": v(36.5, 13.5) * mm, "end": v(33.5, 13.5) * mm});
            skPoint(sketch, "E5.6.2.0", {"position": v(35, 25) * mm});
            skLineSegment(sketch, "E5.6.2.1", {"start": v(36.5, 26.5) * mm, "end": v(36.5, 23.5) * mm});
            skLineSegment(sketch, "E5.6.2.2", {"start": v(36.5, 26.5) * mm, "end": v(33.5, 26.5) * mm});
            skLineSegment(sketch, "E5.6.2.3", {"start": v(33.5, 26.5) * mm, "end": v(33.5, 23.5) * mm});
            skLineSegment(sketch, "E5.6.2.4", {"start": v(36.5, 23.5) * mm, "end": v(33.5, 23.5) * mm});
            skPoint(sketch, "E5.6.3.0", {"position": v(35, 35) * mm});
            skLineSegment(sketch, "E5.6.3.1", {"start": v(36.5, 36.5) * mm, "end": v(36.5, 33.5) * mm});
            skLineSegment(sketch, "E5.6.3.2", {"start": v(36.5, 36.5) * mm, "end": v(33.5, 36.5) * mm});
            skLineSegment(sketch, "E5.6.3.3", {"start": v(33.5, 36.5) * mm, "end": v(33.5, 33.5) * mm});
            skLineSegment(sketch, "E5.6.3.4", {"start": v(36.5, 33.5) * mm, "end": v(33.5, 33.5) * mm});
            skPoint(sketch, "E5.6.4.0", {"position": v(35, 45) * mm});
            skLineSegment(sketch, "E5.6.4.1", {"start": v(36.5, 46.5) * mm, "end": v(36.5, 43.5) * mm});
            skLineSegment(sketch, "E5.6.4.2", {"start": v(36.5, 46.5) * mm, "end": v(33.5, 46.5) * mm});
            skLineSegment(sketch, "E5.6.4.3", {"start": v(33.5, 46.5) * mm, "end": v(33.5, 43.5) * mm});
            skLineSegment(sketch, "E5.6.4.4", {"start": v(36.5, 43.5) * mm, "end": v(33.5, 43.5) * mm});
            skPoint(sketch, "E5.6.5.0", {"position": v(35, 55) * mm});
            skLineSegment(sketch, "E5.6.5.1", {"start": v(36.5, 56.5) * mm, "end": v(36.5, 53.5) * mm});
            skLineSegment(sketch, "E5.6.5.2", {"start": v(36.5, 56.5) * mm, "end": v(33.5, 56.5) * mm});
            skLineSegment(sketch, "E5.6.5.3", {"start": v(33.5, 56.5) * mm, "end": v(33.5, 53.5) * mm});
            skLineSegment(sketch, "E5.6.5.4", {"start": v(36.5, 53.5) * mm, "end": v(33.5, 53.5) * mm});
            skPoint(sketch, "E5.6.6.0", {"position": v(35, 65) * mm});
            skLineSegment(sketch, "E5.6.6.1", {"start": v(36.5, 66.5) * mm, "end": v(36.5, 63.5) * mm});
            skLineSegment(sketch, "E5.6.6.2", {"start": v(36.5, 66.5) * mm, "end": v(33.5, 66.5) * mm});
            skLineSegment(sketch, "E5.6.6.3", {"start": v(33.5, 66.5) * mm, "end": v(33.5, 63.5) * mm});
            skLineSegment(sketch, "E5.6.6.4", {"start": v(36.5, 63.5) * mm, "end": v(33.5, 63.5) * mm});
            skPoint(sketch, "E5.6.7.0", {"position": v(35, 75) * mm});
            skLineSegment(sketch, "E5.6.7.1", {"start": v(36.5, 76.5) * mm, "end": v(36.5, 73.5) * mm});
            skLineSegment(sketch, "E5.6.7.2", {"start": v(36.5, 76.5) * mm, "end": v(33.5, 76.5) * mm});
            skLineSegment(sketch, "E5.6.7.3", {"start": v(33.5, 76.5) * mm, "end": v(33.5, 73.5) * mm});
            skLineSegment(sketch, "E5.6.7.4", {"start": v(36.5, 73.5) * mm, "end": v(33.5, 73.5) * mm});
            skPoint(sketch, "E5.6.8.0", {"position": v(35, 85) * mm});
            skLineSegment(sketch, "E5.6.8.1", {"start": v(36.5, 86.5) * mm, "end": v(36.5, 83.5) * mm});
            skLineSegment(sketch, "E5.6.8.2", {"start": v(36.5, 86.5) * mm, "end": v(33.5, 86.5) * mm});
            skLineSegment(sketch, "E5.6.8.3", {"start": v(33.5, 86.5) * mm, "end": v(33.5, 83.5) * mm});
            skLineSegment(sketch, "E5.6.8.4", {"start": v(36.5, 83.5) * mm, "end": v(33.5, 83.5) * mm});
            skPoint(sketch, "E5.7.0.0", {"position": v(25, 5) * mm});
            skLineSegment(sketch, "E5.7.0.1", {"start": v(26.5, 6.5) * mm, "end": v(26.5, 3.5) * mm});
            skLineSegment(sketch, "E5.7.0.2", {"start": v(26.5, 6.5) * mm, "end": v(23.5, 6.5) * mm});
            skLineSegment(sketch, "E5.7.0.3", {"start": v(23.5, 6.5) * mm, "end": v(23.5, 3.5) * mm});
            skLineSegment(sketch, "E5.7.0.4", {"start": v(26.5, 3.5) * mm, "end": v(23.5, 3.5) * mm});
            skPoint(sketch, "E5.7.1.0", {"position": v(25, 15) * mm});
            skLineSegment(sketch, "E5.7.1.1", {"start": v(26.5, 16.5) * mm, "end": v(26.5, 13.5) * mm});
            skLineSegment(sketch, "E5.7.1.2", {"start": v(26.5, 16.5) * mm, "end": v(23.5, 16.5) * mm});
            skLineSegment(sketch, "E5.7.1.3", {"start": v(23.5, 16.5) * mm, "end": v(23.5, 13.5) * mm});
            skLineSegment(sketch, "E5.7.1.4", {"start": v(26.5, 13.5) * mm, "end": v(23.5, 13.5) * mm});
            skPoint(sketch, "E5.7.2.0", {"position": v(25, 25) * mm});
            skLineSegment(sketch, "E5.7.2.1", {"start": v(26.5, 26.5) * mm, "end": v(26.5, 23.5) * mm});
            skLineSegment(sketch, "E5.7.2.2", {"start": v(26.5, 26.5) * mm, "end": v(23.5, 26.5) * mm});
            skLineSegment(sketch, "E5.7.2.3", {"start": v(23.5, 26.5) * mm, "end": v(23.5, 23.5) * mm});
            skLineSegment(sketch, "E5.7.2.4", {"start": v(26.5, 23.5) * mm, "end": v(23.5, 23.5) * mm});
            skPoint(sketch, "E5.7.3.0", {"position": v(25, 35) * mm});
            skLineSegment(sketch, "E5.7.3.1", {"start": v(26.5, 36.5) * mm, "end": v(26.5, 33.5) * mm});
            skLineSegment(sketch, "E5.7.3.2", {"start": v(26.5, 36.5) * mm, "end": v(23.5, 36.5) * mm});
            skLineSegment(sketch, "E5.7.3.3", {"start": v(23.5, 36.5) * mm, "end": v(23.5, 33.5) * mm});
            skLineSegment(sketch, "E5.7.3.4", {"start": v(26.5, 33.5) * mm, "end": v(23.5, 33.5) * mm});
            skPoint(sketch, "E5.7.4.0", {"position": v(25, 45) * mm});
            skLineSegment(sketch, "E5.7.4.1", {"start": v(26.5, 46.5) * mm, "end": v(26.5, 43.5) * mm});
            skLineSegment(sketch, "E5.7.4.2", {"start": v(26.5, 46.5) * mm, "end": v(23.5, 46.5) * mm});
            skLineSegment(sketch, "E5.7.4.3", {"start": v(23.5, 46.5) * mm, "end": v(23.5, 43.5) * mm});
            skLineSegment(sketch, "E5.7.4.4", {"start": v(26.5, 43.5) * mm, "end": v(23.5, 43.5) * mm});
            skPoint(sketch, "E5.7.5.0", {"position": v(25, 55) * mm});
            skLineSegment(sketch, "E5.7.5.1", {"start": v(26.5, 56.5) * mm, "end": v(26.5, 53.5) * mm});
            skLineSegment(sketch, "E5.7.5.2", {"start": v(26.5, 56.5) * mm, "end": v(23.5, 56.5) * mm});
            skLineSegment(sketch, "E5.7.5.3", {"start": v(23.5, 56.5) * mm, "end": v(23.5, 53.5) * mm});
            skLineSegment(sketch, "E5.7.5.4", {"start": v(26.5, 53.5) * mm, "end": v(23.5, 53.5) * mm});
            skPoint(sketch, "E5.7.6.0", {"position": v(25, 65) * mm});
            skLineSegment(sketch, "E5.7.6.1", {"start": v(26.5, 66.5) * mm, "end": v(26.5, 63.5) * mm});
            skLineSegment(sketch, "E5.7.6.2", {"start": v(26.5, 66.5) * mm, "end": v(23.5, 66.5) * mm});
            skLineSegment(sketch, "E5.7.6.3", {"start": v(23.5, 66.5) * mm, "end": v(23.5, 63.5) * mm});
            skLineSegment(sketch, "E5.7.6.4", {"start": v(26.5, 63.5) * mm, "end": v(23.5, 63.5) * mm});
            skPoint(sketch, "E5.7.7.0", {"position": v(25, 75) * mm});
            skLineSegment(sketch, "E5.7.7.1", {"start": v(26.5, 76.5) * mm, "end": v(26.5, 73.5) * mm});
            skLineSegment(sketch, "E5.7.7.2", {"start": v(26.5, 76.5) * mm, "end": v(23.5, 76.5) * mm});
            skLineSegment(sketch, "E5.7.7.3", {"start": v(23.5, 76.5) * mm, "end": v(23.5, 73.5) * mm});
            skLineSegment(sketch, "E5.7.7.4", {"start": v(26.5, 73.5) * mm, "end": v(23.5, 73.5) * mm});
            skPoint(sketch, "E5.7.8.0", {"position": v(25, 85) * mm});
            skLineSegment(sketch, "E5.7.8.1", {"start": v(26.5, 86.5) * mm, "end": v(26.5, 83.5) * mm});
            skLineSegment(sketch, "E5.7.8.2", {"start": v(26.5, 86.5) * mm, "end": v(23.5, 86.5) * mm});
            skLineSegment(sketch, "E5.7.8.3", {"start": v(23.5, 86.5) * mm, "end": v(23.5, 83.5) * mm});
            skLineSegment(sketch, "E5.7.8.4", {"start": v(26.5, 83.5) * mm, "end": v(23.5, 83.5) * mm});
            skPoint(sketch, "E5.8.0.0", {"position": v(15, 5) * mm});
            skLineSegment(sketch, "E5.8.0.1", {"start": v(16.5, 6.5) * mm, "end": v(16.5, 3.5) * mm});
            skLineSegment(sketch, "E5.8.0.2", {"start": v(16.5, 6.5) * mm, "end": v(13.5, 6.5) * mm});
            skLineSegment(sketch, "E5.8.0.3", {"start": v(13.5, 6.5) * mm, "end": v(13.5, 3.5) * mm});
            skLineSegment(sketch, "E5.8.0.4", {"start": v(16.5, 3.5) * mm, "end": v(13.5, 3.5) * mm});
            skPoint(sketch, "E5.8.1.0", {"position": v(15, 15) * mm});
            skLineSegment(sketch, "E5.8.1.1", {"start": v(16.5, 16.5) * mm, "end": v(16.5, 13.5) * mm});
            skLineSegment(sketch, "E5.8.1.2", {"start": v(16.5, 16.5) * mm, "end": v(13.5, 16.5) * mm});
            skLineSegment(sketch, "E5.8.1.3", {"start": v(13.5, 16.5) * mm, "end": v(13.5, 13.5) * mm});
            skLineSegment(sketch, "E5.8.1.4", {"start": v(16.5, 13.5) * mm, "end": v(13.5, 13.5) * mm});
            skPoint(sketch, "E5.8.2.0", {"position": v(15, 25) * mm});
            skLineSegment(sketch, "E5.8.2.1", {"start": v(16.5, 26.5) * mm, "end": v(16.5, 23.5) * mm});
            skLineSegment(sketch, "E5.8.2.2", {"start": v(16.5, 26.5) * mm, "end": v(13.5, 26.5) * mm});
            skLineSegment(sketch, "E5.8.2.3", {"start": v(13.5, 26.5) * mm, "end": v(13.5, 23.5) * mm});
            skLineSegment(sketch, "E5.8.2.4", {"start": v(16.5, 23.5) * mm, "end": v(13.5, 23.5) * mm});
            skPoint(sketch, "E5.8.3.0", {"position": v(15, 35) * mm});
            skLineSegment(sketch, "E5.8.3.1", {"start": v(16.5, 36.5) * mm, "end": v(16.5, 33.5) * mm});
            skLineSegment(sketch, "E5.8.3.2", {"start": v(16.5, 36.5) * mm, "end": v(13.5, 36.5) * mm});
            skLineSegment(sketch, "E5.8.3.3", {"start": v(13.5, 36.5) * mm, "end": v(13.5, 33.5) * mm});
            skLineSegment(sketch, "E5.8.3.4", {"start": v(16.5, 33.5) * mm, "end": v(13.5, 33.5) * mm});
            skPoint(sketch, "E5.8.4.0", {"position": v(15, 45) * mm});
            skLineSegment(sketch, "E5.8.4.1", {"start": v(16.5, 46.5) * mm, "end": v(16.5, 43.5) * mm});
            skLineSegment(sketch, "E5.8.4.2", {"start": v(16.5, 46.5) * mm, "end": v(13.5, 46.5) * mm});
            skLineSegment(sketch, "E5.8.4.3", {"start": v(13.5, 46.5) * mm, "end": v(13.5, 43.5) * mm});
            skLineSegment(sketch, "E5.8.4.4", {"start": v(16.5, 43.5) * mm, "end": v(13.5, 43.5) * mm});
            skPoint(sketch, "E5.8.5.0", {"position": v(15, 55) * mm});
            skLineSegment(sketch, "E5.8.5.1", {"start": v(16.5, 56.5) * mm, "end": v(16.5, 53.5) * mm});
            skLineSegment(sketch, "E5.8.5.2", {"start": v(16.5, 56.5) * mm, "end": v(13.5, 56.5) * mm});
            skLineSegment(sketch, "E5.8.5.3", {"start": v(13.5, 56.5) * mm, "end": v(13.5, 53.5) * mm});
            skLineSegment(sketch, "E5.8.5.4", {"start": v(16.5, 53.5) * mm, "end": v(13.5, 53.5) * mm});
            skPoint(sketch, "E5.8.6.0", {"position": v(15, 65) * mm});
            skLineSegment(sketch, "E5.8.6.1", {"start": v(16.5, 66.5) * mm, "end": v(16.5, 63.5) * mm});
            skLineSegment(sketch, "E5.8.6.2", {"start": v(16.5, 66.5) * mm, "end": v(13.5, 66.5) * mm});
            skLineSegment(sketch, "E5.8.6.3", {"start": v(13.5, 66.5) * mm, "end": v(13.5, 63.5) * mm});
            skLineSegment(sketch, "E5.8.6.4", {"start": v(16.5, 63.5) * mm, "end": v(13.5, 63.5) * mm});
            skPoint(sketch, "E5.8.7.0", {"position": v(15, 75) * mm});
            skLineSegment(sketch, "E5.8.7.1", {"start": v(16.5, 76.5) * mm, "end": v(16.5, 73.5) * mm});
            skLineSegment(sketch, "E5.8.7.2", {"start": v(16.5, 76.5) * mm, "end": v(13.5, 76.5) * mm});
            skLineSegment(sketch, "E5.8.7.3", {"start": v(13.5, 76.5) * mm, "end": v(13.5, 73.5) * mm});
            skLineSegment(sketch, "E5.8.7.4", {"start": v(16.5, 73.5) * mm, "end": v(13.5, 73.5) * mm});
            skPoint(sketch, "E5.8.8.0", {"position": v(15, 85) * mm});
            skLineSegment(sketch, "E5.8.8.1", {"start": v(16.5, 86.5) * mm, "end": v(16.5, 83.5) * mm});
            skLineSegment(sketch, "E5.8.8.2", {"start": v(16.5, 86.5) * mm, "end": v(13.5, 86.5) * mm});
            skLineSegment(sketch, "E5.8.8.3", {"start": v(13.5, 86.5) * mm, "end": v(13.5, 83.5) * mm});
            skLineSegment(sketch, "E5.8.8.4", {"start": v(16.5, 83.5) * mm, "end": v(13.5, 83.5) * mm});
            skLineSegment(sketch, "E5.direction1", {"start": v(95, 5) * mm, "end": v(85, 5) * mm, "construction": true});
            skLineSegment(sketch, "E5.direction2", {"start": v(95, 5) * mm, "end": v(95, 15) * mm, "construction": true});
            skPoint(sketch, "E6.0.9.0", {"position": v(5, 5) * mm});
            skLineSegment(sketch, "E6.1.9.0", {"start": v(6.5, 6.5) * mm, "end": v(6.5, 3.5) * mm});
            skLineSegment(sketch, "E6.4.9.0", {"start": v(6.5, 6.5) * mm, "end": v(3.5, 6.5) * mm});
            skLineSegment(sketch, "E6.7.9.0", {"start": v(3.5, 6.5) * mm, "end": v(3.5, 3.5) * mm});
            skLineSegment(sketch, "E6.10.9.0", {"start": v(6.5, 3.5) * mm, "end": v(3.5, 3.5) * mm});
            skPoint(sketch, "E6.0.9.1", {"position": v(5, 15) * mm});
            skLineSegment(sketch, "E6.1.9.1", {"start": v(6.5, 16.5) * mm, "end": v(6.5, 13.5) * mm});
            skLineSegment(sketch, "E6.4.9.1", {"start": v(6.5, 16.5) * mm, "end": v(3.5, 16.5) * mm});
            skLineSegment(sketch, "E6.7.9.1", {"start": v(3.5, 16.5) * mm, "end": v(3.5, 13.5) * mm});
            skLineSegment(sketch, "E6.10.9.1", {"start": v(6.5, 13.5) * mm, "end": v(3.5, 13.5) * mm});
            skPoint(sketch, "E6.0.9.2", {"position": v(5, 25) * mm});
            skLineSegment(sketch, "E6.1.9.2", {"start": v(6.5, 26.5) * mm, "end": v(6.5, 23.5) * mm});
            skLineSegment(sketch, "E6.4.9.2", {"start": v(6.5, 26.5) * mm, "end": v(3.5, 26.5) * mm});
            skLineSegment(sketch, "E6.7.9.2", {"start": v(3.5, 26.5) * mm, "end": v(3.5, 23.5) * mm});
            skLineSegment(sketch, "E6.10.9.2", {"start": v(6.5, 23.5) * mm, "end": v(3.5, 23.5) * mm});
            skPoint(sketch, "E6.0.9.3", {"position": v(5, 35) * mm});
            skLineSegment(sketch, "E6.1.9.3", {"start": v(6.5, 36.5) * mm, "end": v(6.5, 33.5) * mm});
            skLineSegment(sketch, "E6.4.9.3", {"start": v(6.5, 36.5) * mm, "end": v(3.5, 36.5) * mm});
            skLineSegment(sketch, "E6.7.9.3", {"start": v(3.5, 36.5) * mm, "end": v(3.5, 33.5) * mm});
            skLineSegment(sketch, "E6.10.9.3", {"start": v(6.5, 33.5) * mm, "end": v(3.5, 33.5) * mm});
            skPoint(sketch, "E6.0.9.4", {"position": v(5, 45) * mm});
            skLineSegment(sketch, "E6.1.9.4", {"start": v(6.5, 46.5) * mm, "end": v(6.5, 43.5) * mm});
            skLineSegment(sketch, "E6.4.9.4", {"start": v(6.5, 46.5) * mm, "end": v(3.5, 46.5) * mm});
            skLineSegment(sketch, "E6.7.9.4", {"start": v(3.5, 46.5) * mm, "end": v(3.5, 43.5) * mm});
            skLineSegment(sketch, "E6.10.9.4", {"start": v(6.5, 43.5) * mm, "end": v(3.5, 43.5) * mm});
            skPoint(sketch, "E6.0.9.5", {"position": v(5, 55) * mm});
            skLineSegment(sketch, "E6.1.9.5", {"start": v(6.5, 56.5) * mm, "end": v(6.5, 53.5) * mm});
            skLineSegment(sketch, "E6.4.9.5", {"start": v(6.5, 56.5) * mm, "end": v(3.5, 56.5) * mm});
            skLineSegment(sketch, "E6.7.9.5", {"start": v(3.5, 56.5) * mm, "end": v(3.5, 53.5) * mm});
            skLineSegment(sketch, "E6.10.9.5", {"start": v(6.5, 53.5) * mm, "end": v(3.5, 53.5) * mm});
            skPoint(sketch, "E6.0.9.6", {"position": v(5, 65) * mm});
            skLineSegment(sketch, "E6.1.9.6", {"start": v(6.5, 66.5) * mm, "end": v(6.5, 63.5) * mm});
            skLineSegment(sketch, "E6.4.9.6", {"start": v(6.5, 66.5) * mm, "end": v(3.5, 66.5) * mm});
            skLineSegment(sketch, "E6.7.9.6", {"start": v(3.5, 66.5) * mm, "end": v(3.5, 63.5) * mm});
            skLineSegment(sketch, "E6.10.9.6", {"start": v(6.5, 63.5) * mm, "end": v(3.5, 63.5) * mm});
            skPoint(sketch, "E6.0.9.7", {"position": v(5, 75) * mm});
            skLineSegment(sketch, "E6.1.9.7", {"start": v(6.5, 76.5) * mm, "end": v(6.5, 73.5) * mm});
            skLineSegment(sketch, "E6.4.9.7", {"start": v(6.5, 76.5) * mm, "end": v(3.5, 76.5) * mm});
            skLineSegment(sketch, "E6.7.9.7", {"start": v(3.5, 76.5) * mm, "end": v(3.5, 73.5) * mm});
            skLineSegment(sketch, "E6.10.9.7", {"start": v(6.5, 73.5) * mm, "end": v(3.5, 73.5) * mm});
            skPoint(sketch, "E6.0.9.8", {"position": v(5, 85) * mm});
            skLineSegment(sketch, "E6.1.9.8", {"start": v(6.5, 86.5) * mm, "end": v(6.5, 83.5) * mm});
            skLineSegment(sketch, "E6.4.9.8", {"start": v(6.5, 86.5) * mm, "end": v(3.5, 86.5) * mm});
            skLineSegment(sketch, "E6.7.9.8", {"start": v(3.5, 86.5) * mm, "end": v(3.5, 83.5) * mm});
            skLineSegment(sketch, "E6.10.9.8", {"start": v(6.5, 83.5) * mm, "end": v(3.5, 83.5) * mm});
            skPoint(sketch, "E7.0.0.9", {"position": v(95, 95) * mm});
            skLineSegment(sketch, "E7.1.0.9", {"start": v(96.5, 96.5) * mm, "end": v(96.5, 93.5) * mm});
            skLineSegment(sketch, "E7.4.0.9", {"start": v(96.5, 96.5) * mm, "end": v(93.5, 96.5) * mm});
            skLineSegment(sketch, "E7.7.0.9", {"start": v(93.5, 96.5) * mm, "end": v(93.5, 93.5) * mm});
            skLineSegment(sketch, "E7.10.0.9", {"start": v(96.5, 93.5) * mm, "end": v(93.5, 93.5) * mm});
            skPoint(sketch, "E7.0.1.9", {"position": v(85, 95) * mm});
            skLineSegment(sketch, "E7.1.1.9", {"start": v(86.5, 96.5) * mm, "end": v(86.5, 93.5) * mm});
            skLineSegment(sketch, "E7.4.1.9", {"start": v(86.5, 96.5) * mm, "end": v(83.5, 96.5) * mm});
            skLineSegment(sketch, "E7.7.1.9", {"start": v(83.5, 96.5) * mm, "end": v(83.5, 93.5) * mm});
            skLineSegment(sketch, "E7.10.1.9", {"start": v(86.5, 93.5) * mm, "end": v(83.5, 93.5) * mm});
            skPoint(sketch, "E7.0.2.9", {"position": v(75, 95) * mm});
            skLineSegment(sketch, "E7.1.2.9", {"start": v(76.5, 96.5) * mm, "end": v(76.5, 93.5) * mm});
            skLineSegment(sketch, "E7.4.2.9", {"start": v(76.5, 96.5) * mm, "end": v(73.5, 96.5) * mm});
            skLineSegment(sketch, "E7.7.2.9", {"start": v(73.5, 96.5) * mm, "end": v(73.5, 93.5) * mm});
            skLineSegment(sketch, "E7.10.2.9", {"start": v(76.5, 93.5) * mm, "end": v(73.5, 93.5) * mm});
            skPoint(sketch, "E7.0.3.9", {"position": v(65, 95) * mm});
            skLineSegment(sketch, "E7.1.3.9", {"start": v(66.5, 96.5) * mm, "end": v(66.5, 93.5) * mm});
            skLineSegment(sketch, "E7.4.3.9", {"start": v(66.5, 96.5) * mm, "end": v(63.5, 96.5) * mm});
            skLineSegment(sketch, "E7.7.3.9", {"start": v(63.5, 96.5) * mm, "end": v(63.5, 93.5) * mm});
            skLineSegment(sketch, "E7.10.3.9", {"start": v(66.5, 93.5) * mm, "end": v(63.5, 93.5) * mm});
            skPoint(sketch, "E7.0.4.9", {"position": v(55, 95) * mm});
            skLineSegment(sketch, "E7.1.4.9", {"start": v(56.5, 96.5) * mm, "end": v(56.5, 93.5) * mm});
            skLineSegment(sketch, "E7.4.4.9", {"start": v(56.5, 96.5) * mm, "end": v(53.5, 96.5) * mm});
            skLineSegment(sketch, "E7.7.4.9", {"start": v(53.5, 96.5) * mm, "end": v(53.5, 93.5) * mm});
            skLineSegment(sketch, "E7.10.4.9", {"start": v(56.5, 93.5) * mm, "end": v(53.5, 93.5) * mm});
            skPoint(sketch, "E7.0.5.9", {"position": v(45, 95) * mm});
            skLineSegment(sketch, "E7.1.5.9", {"start": v(46.5, 96.5) * mm, "end": v(46.5, 93.5) * mm});
            skLineSegment(sketch, "E7.4.5.9", {"start": v(46.5, 96.5) * mm, "end": v(43.5, 96.5) * mm});
            skLineSegment(sketch, "E7.7.5.9", {"start": v(43.5, 96.5) * mm, "end": v(43.5, 93.5) * mm});
            skLineSegment(sketch, "E7.10.5.9", {"start": v(46.5, 93.5) * mm, "end": v(43.5, 93.5) * mm});
            skPoint(sketch, "E7.0.6.9", {"position": v(35, 95) * mm});
            skLineSegment(sketch, "E7.1.6.9", {"start": v(36.5, 96.5) * mm, "end": v(36.5, 93.5) * mm});
            skLineSegment(sketch, "E7.4.6.9", {"start": v(36.5, 96.5) * mm, "end": v(33.5, 96.5) * mm});
            skLineSegment(sketch, "E7.7.6.9", {"start": v(33.5, 96.5) * mm, "end": v(33.5, 93.5) * mm});
            skLineSegment(sketch, "E7.10.6.9", {"start": v(36.5, 93.5) * mm, "end": v(33.5, 93.5) * mm});
            skPoint(sketch, "E7.0.7.9", {"position": v(25, 95) * mm});
            skLineSegment(sketch, "E7.1.7.9", {"start": v(26.5, 96.5) * mm, "end": v(26.5, 93.5) * mm});
            skLineSegment(sketch, "E7.4.7.9", {"start": v(26.5, 96.5) * mm, "end": v(23.5, 96.5) * mm});
            skLineSegment(sketch, "E7.7.7.9", {"start": v(23.5, 96.5) * mm, "end": v(23.5, 93.5) * mm});
            skLineSegment(sketch, "E7.10.7.9", {"start": v(26.5, 93.5) * mm, "end": v(23.5, 93.5) * mm});
            skPoint(sketch, "E7.0.8.9", {"position": v(15, 95) * mm});
            skLineSegment(sketch, "E7.1.8.9", {"start": v(16.5, 96.5) * mm, "end": v(16.5, 93.5) * mm});
            skLineSegment(sketch, "E7.4.8.9", {"start": v(16.5, 96.5) * mm, "end": v(13.5, 96.5) * mm});
            skLineSegment(sketch, "E7.7.8.9", {"start": v(13.5, 96.5) * mm, "end": v(13.5, 93.5) * mm});
            skLineSegment(sketch, "E7.10.8.9", {"start": v(16.5, 93.5) * mm, "end": v(13.5, 93.5) * mm});
            skPoint(sketch, "E7.0.9.9", {"position": v(5, 95) * mm});
            skLineSegment(sketch, "E7.1.9.9", {"start": v(6.5, 96.5) * mm, "end": v(6.5, 93.5) * mm});
            skLineSegment(sketch, "E7.4.9.9", {"start": v(6.5, 96.5) * mm, "end": v(3.5, 96.5) * mm});
            skLineSegment(sketch, "E7.7.9.9", {"start": v(3.5, 96.5) * mm, "end": v(3.5, 93.5) * mm});
            skLineSegment(sketch, "E7.10.9.9", {"start": v(6.5, 93.5) * mm, "end": v(3.5, 93.5) * mm});
            skSolve(sketch);
        }
        {
            var Q0;
            Q0=qCreatedBy(makeId("Top.planeOp"),FACE);
            cPlane(context, id + "F6", {"entities" : qUnion([Q0]), "cplaneType" : CPlaneType.OFFSET, "offset" : 2 * mm, "width" : 150 * mm, "height" : 150 * mm});
        }
    });
